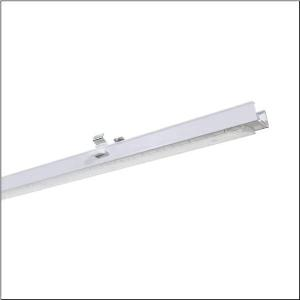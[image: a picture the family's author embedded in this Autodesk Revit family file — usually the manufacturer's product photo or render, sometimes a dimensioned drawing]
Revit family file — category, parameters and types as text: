
# Revit family: trunking_flex_31_51re18mb4cb
name_source: partatom
category: Lighting Fixtures
units: mm (PartAtom-declared; Revit-internal decimal feet)

## family parameters
Cut with Voids When Loaded = No
Host = Face
Light Source = No
Part Type = Normal
Room Calculation Point = No
Round Connector Dimension = Use Diameter
Shared = No

## types (1)
- --- (1 x LED, 11500 lm, 66 W, 4000K)
    Apparent Load = 66 VA
    CIE Flux Codes = 71 89 97 97 100
    Color Rendering = 80
    Color Temperature = 4000K
    Default Elevation = 1800 mm
    Description = Trunking Flex 31, luminaire insert, of extruded aluminium section, coated, traffic white (RAL 9016), length: 1.472mm, width: 91mm, height: 53mm, LED rated luminous flux: 11.500lm, light colour: 840, control gear: ON/OFF Multilumen, with system connector: socket, mains connection: 220..240V, AC, 50/60Hz, rated input power: 66W, connected load according to luminous flux setting (19/24/32/37/47/52/60/66W), luminous flux adjustable on luminaire in eight steps (3450/4380/5800/6700/8350/9200/10500/11500lm ), primary light control with lens, of plastic, primary optical cover: cover, of PMMA, light emission: direct distribution, protection rating (complete): IP20, insulation class (complete): insulation class I (protective earthing), certification: CE, UKCA, impact resistance: IK02, permissible ambient temperature for indoor applications: -20..+40°C, packaging unit: 1 piece
    Height = 58 mm
    Lamp = 1 x LED
    Lamp Light Flux = 11500 lm
    Lamp Power = 66 W
    Lamp count = 1
    Length = 1472 mm
    Luminous efficacy = 174 lm/W
    Manufacturer = Siteco
    ModVariant = No
    Model = 51RE18MB4CB
    Mounting Place = Ceiling
    Mounting Type = Pendant
    Number of Poles = 1
    OnlyDefault = Yes
    Power Factor = 1
    Product Name = Trunking Flex 31
    Product group = luminaire insert
    ProductGroupID = 901
    Protection Class = Protection class I
    Protection Degree = IP 20
    RLX_Detail_Level = 1
    RLX_Emergency_Light_Flux = 0 lm
    RLX_Emergency_Type = 0
    RLX_Emergency_Type_DB = No
    RlxData = <blob elided: 21157 chars, md5=7d0a289f>
    Socket = socket
    Standby Power = 0 W
    System Light Flux = 11500 lm
    System Power = 66 W
    Type Comments = factory setting: luminous flux: 100 % | (ON | ON | ON)
    Type Image = l_1266702.jpg
    URL = http://relux.com
    VarID = @adj_018561
    Voltage = 0 V
    Weight = 0.00 kg
    Width = 65 mm

## geometry (parser evidence)
native form markers: Blend x4, Sweep x12
no freeform markers — native parametric forms only
